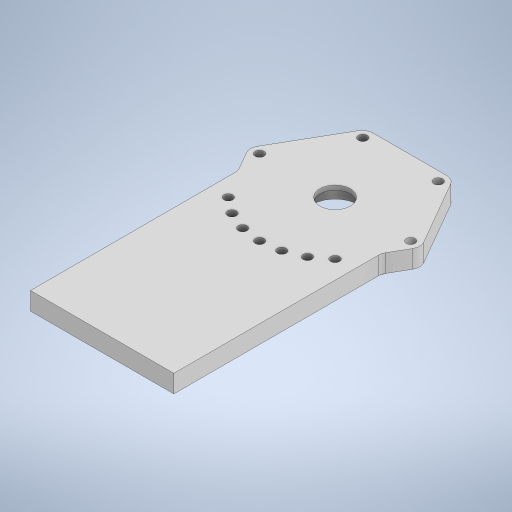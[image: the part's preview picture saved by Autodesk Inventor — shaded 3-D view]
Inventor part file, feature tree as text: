
AUTODESK INVENTOR PART (.ipt)
format: ipt  version: 2024 (Build 280153000, 153)  size: 373,248 bytes
history: native  units: mm
features: extrude x8, sketch x8, fillet x1, projected_geometry x1
ambient origin geometry x8: Origin, YZ Plane, XZ Plane, XY Plane, X Axis, Y Axis, Z Axis, Center Point
bodies: Solid1 (feature_tree)
feature tree (18):
  extrude  "Extrusion1"  Depth=10.0mm
  extrude  "Extrusion2"  Depth=20.0mm TaperAngle=0.0deg
  sketch  "Sketch3"  dims[d8=34.0mm d9=5.0mm d10=0.0mm]
  sketch  "Sketch4"  dims[d12=60.0mm d13=360.0deg d14=22.0mm d15=0.0mm]
  extrude  "Extrusion3"  Depth=5.0mm TaperAngle=0.0deg
  extrude  "Extrusion4"  Depth=22.0mm TaperAngle=0.0deg
  extrude  "Extrusion5"  Depth=20.0mm TaperAngle=0.0deg
  fillet  "Fillet1"  Radius=150.0mm
  extrude  "Extrusion6"  Depth=12.0mm
  extrude  "Extrusion7"  Depth=20.0mm
  extrude  "Extrusion8"  Depth=20.0mm
  sketch  "Sketch1"  dims[d0=250.0mm d1=160.0mm d2=160.0mm d3=10.0mm d4=52.0mm]
  sketch  "Sketch2"  dims[d5=80.0mm d6=20.0mm d7=0.0mm]
  sketch  "Sketch5"  dims[d17=60.0mm d18=360.0deg d19=20.0mm d20=0.0mm d21=150.0mm]
  sketch  "Sketch6"  dims[d22=5.0mm d23=0.0mm d24=12.0mm]
  projected_geometry  "Projected Loop1"
  sketch  "Sketch7"  dims[d25=20.0mm d26=20.0mm]
  sketch  "Sketch8"  dims[d27=12.0mm d28=0.0mm d29=84.286mm d30=10.0mm d31=240.0mm d33=360.0deg d35=39.0mm d36=0.0mm d37=20.0mm d38=0.0mm]
